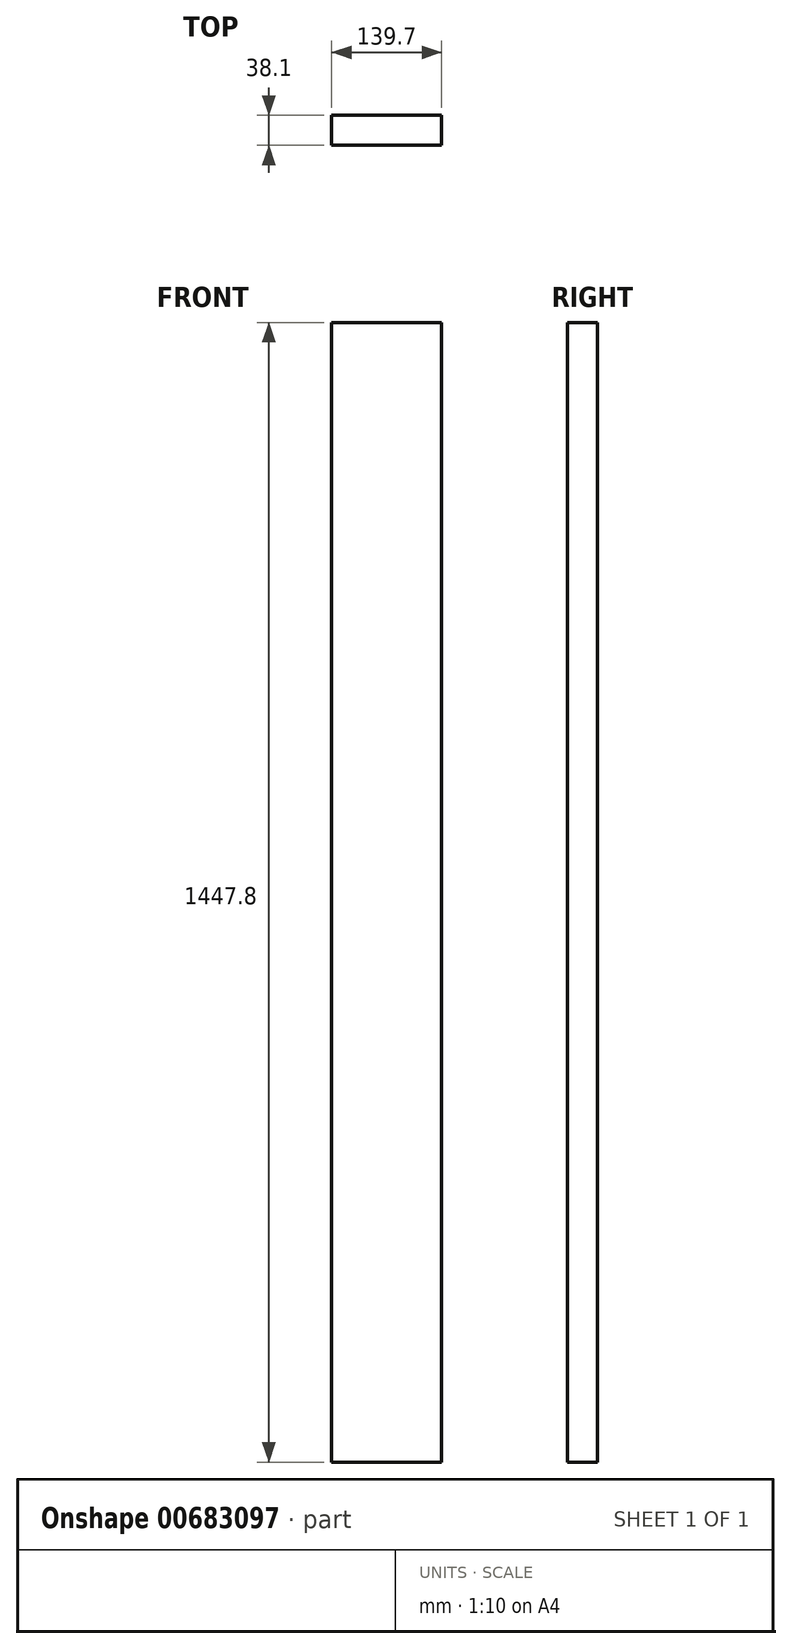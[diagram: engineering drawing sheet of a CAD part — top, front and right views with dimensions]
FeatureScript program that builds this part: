
annotation { "Feature Type Name" : "Feature", "Feature Type Description" : "" }
export const myFeature = defineFeature(function(context is Context, id is Id, definition is map)
    precondition{}
    {
        {
            var Q0;
            Q0=qCreatedBy(makeId("Top.planeOp"),FACE);
            var sketch = newSketch(context, id + "F0", { "sketchPlane" : qUnion([Q0])});
            skLineSegment(sketch, "E0.bottom", {"start": v(69.85, 19.05) * mm, "end": v(-69.85, 19.05) * mm});
            skLineSegment(sketch, "E0.top", {"start": v(69.85, -19.05) * mm, "end": v(-69.85, -19.05) * mm});
            skLineSegment(sketch, "E0.left", {"start": v(69.85, 19.05) * mm, "end": v(69.85, -19.05) * mm});
            skLineSegment(sketch, "E0.right", {"start": v(-69.85, 19.05) * mm, "end": v(-69.85, -19.05) * mm});
            skPoint(sketch, "E0.middle", {"position": v(0, 0) * mm});
            skSolve(sketch);
        }
        {
            var Q0;
            Q0=makeQuery(id+"F0.imprint","IMPRINT",FACE,{"disambiguationData":[TD([[makeQuery(id+"F0.imprint","IMPRINT",EDGE,{"derivedFrom":sQuery(id+"F0.wireOp",EDGE,"E0.bottom")}),1.0]])]});
            extrude(context, id + "F1", {"entities" : qUnion([Q0]), "depth" : 1447.8 * mm, "offsetDistance" : 25.4 * mm});
        }
    });
